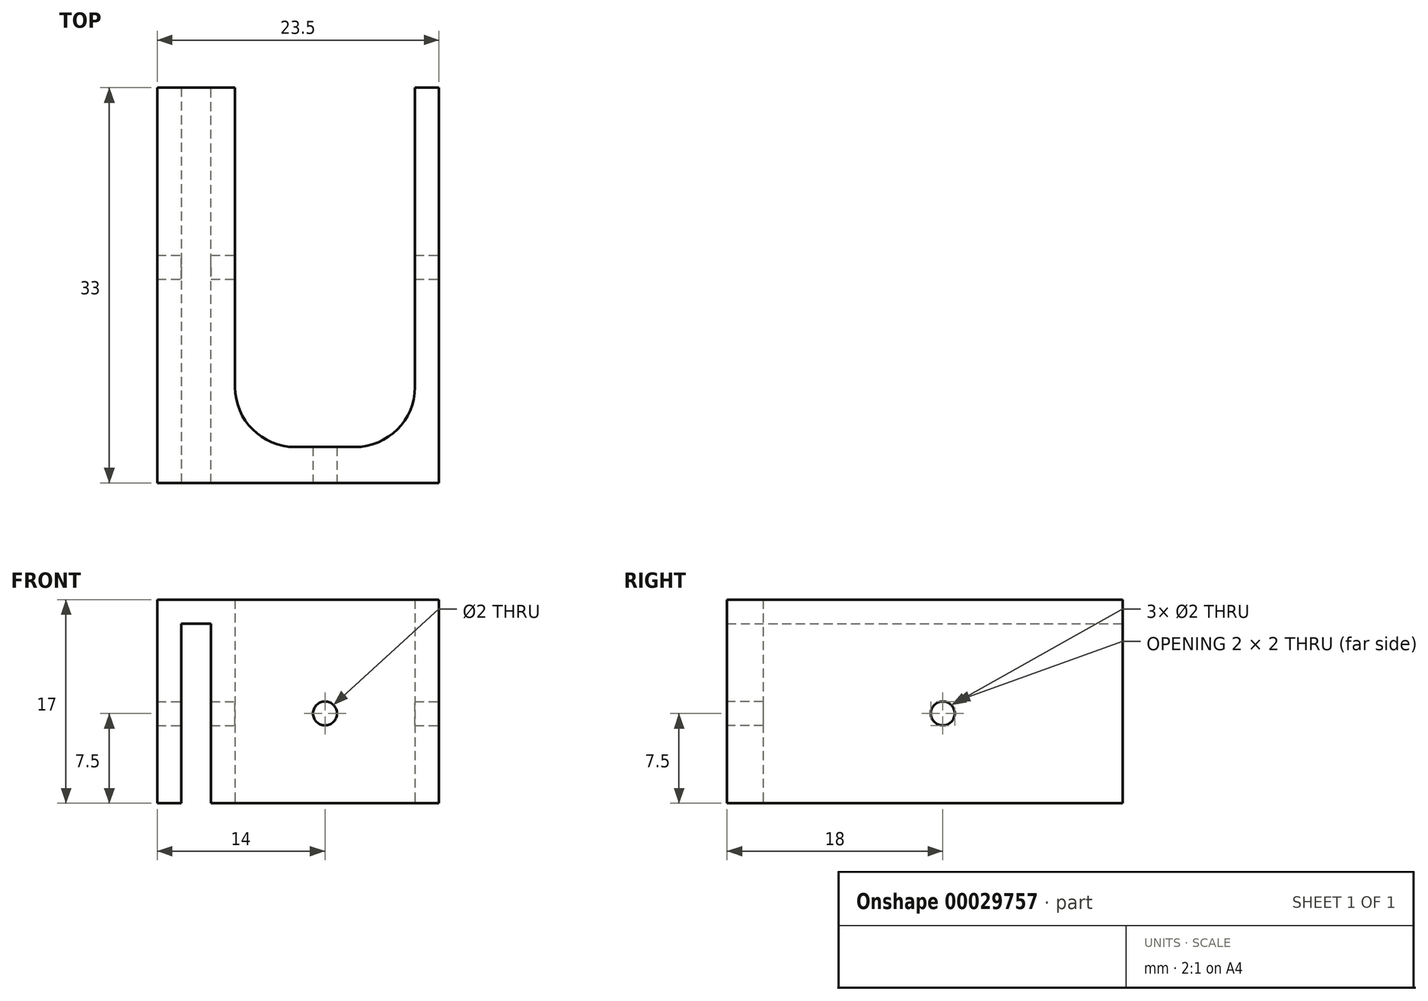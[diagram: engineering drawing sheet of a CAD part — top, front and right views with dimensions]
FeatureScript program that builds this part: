
annotation { "Feature Type Name" : "Feature", "Feature Type Description" : "" }
export const myFeature = defineFeature(function(context is Context, id is Id, definition is map)
    precondition{}
    {
        {
            var Q0;
            Q0=qCreatedBy(makeId("Top.planeOp"),FACE);
            var sketch = newSketch(context, id + "F0", { "sketchPlane" : qUnion([Q0])});
            skLineSegment(sketch, "E0.top", {"start": v(0, 33) * mm, "end": v(-2, 33) * mm});
            skLineSegment(sketch, "E0.left", {"start": v(0, 0) * mm, "end": v(0, 33) * mm});
            skLineSegment(sketch, "E0.right", {"start": v(-19, 6) * mm, "end": v(-19, 33) * mm});
            skLineSegment(sketch, "E1.top", {"start": v(-17, 3) * mm, "end": v(-2, 3) * mm});
            skLineSegment(sketch, "E1.left", {"start": v(-17, 33) * mm, "end": v(-17, 3) * mm});
            skLineSegment(sketch, "E1.right", {"start": v(-2, 33) * mm, "end": v(-2, 3) * mm});
            skLineSegment(sketch, "E2.trimOffspring", {"start": v(-17, 33) * mm, "end": v(-19, 33) * mm});
            skLineSegment(sketch, "E3", {"start": v(-19, 0) * mm, "end": v(0, 0) * mm});
            skPoint(sketch, "E4.end.orphan", {"position": v(12, 0) * mm});
            skPoint(sketch, "E5.end.orphan", {"position": v(-31, 0) * mm});
            skLineSegment(sketch, "E6", {"start": v(-19, 0) * mm, "end": v(-23.5, 0) * mm});
            skLineSegment(sketch, "E7", {"start": v(-23.5, 0) * mm, "end": v(-23.5, 33) * mm});
            skLineSegment(sketch, "E8", {"start": v(-23.5, 33) * mm, "end": v(-21.5, 33) * mm});
            skLineSegment(sketch, "E9", {"start": v(-21.5, 33) * mm, "end": v(-21.5, 6) * mm});
            skLineSegment(sketch, "E10", {"start": v(-19, 6) * mm, "end": v(-21.5, 6) * mm});
            skPoint(sketch, "E11.orphan", {"position": v(-21.5, 3) * mm});
            skSolve(sketch);
        }
        {
            var Q0;
            Q0=makeQuery(id+"F0.imprint","IMPRINT",FACE,{"disambiguationData":[TD([[makeQuery(id+"F0.imprint","IMPRINT",EDGE,{"derivedFrom":sQuery(id+"F0.wireOp",EDGE,"E0.top")}),1.0]])]});
            extrude(context, id + "F1", {"entities" : qUnion([Q0]), "depth" : 15 * mm});
        }
        {
            var Q0;
            Q0=makeQuery(id+"F1.opExtrude","SWEPT_FACE",FACE,{"disambiguationData":[OSD([sQuery(id+"F0.wireOp",EDGE,"E0.left")])]});
            var sketch = newSketch(context, id + "F2", { "sketchPlane" : qUnion([Q0])});
            skCircle(sketch, "E12", {"center": v(18, 7.5) * mm, "radius": 1 * mm});
            skSolve(sketch);
        }
        {
            var Q0;
            Q0=qSketchRegion(id+"F2",true);
            extrude(context, id + "F3", {"entities" : qUnion([Q0]), "operationType" : NewBodyOperationType.REMOVE, "oppositeDirection" : true, "depth" : 25 * mm});
        }
        {
            var Q0;
            Q0=makeQuery(id+"F1.opExtrude","SWEPT_FACE",FACE,{"disambiguationData":[OSD([sQuery(id+"F0.wireOp",EDGE,"E3"),sQuery(id+"F0.wireOp",EDGE,"E5"),sQuery(id+"F0.wireOp",EDGE,"KW2I9wrd-rldA-EDLi-8j01-u2Y36levhrCV")])]});
            var sketch = newSketch(context, id + "F4", { "sketchPlane" : qUnion([Q0])});
            skCircle(sketch, "E13", {"center": v(-9.5, 7.5) * mm, "radius": 1 * mm});
            skCircle(sketch, "E14", {"center": v(-25, 7.5) * mm, "radius": 1 * mm});
            skCircle(sketch, "E15", {"center": v(6, 7.5) * mm, "radius": 1 * mm});
            skLineSegment(sketch, "E16.0", {"start": v(12, 15) * mm, "end": v(12, 0) * mm});
            skCircle(sketch, "E17", {"center": v(-31, 7.5) * mm, "radius": 0.5 * mm});
            skCircle(sketch, "E18", {"center": v(12, 7.5) * mm, "radius": 0.5 * mm});
            skLineSegment(sketch, "E19.0", {"start": v(12, 15) * mm, "end": v(-31, 15) * mm});
            skSolve(sketch);
        }
        {
            var Q0;
            Q0=qSketchRegion(id+"F4",true);
            extrude(context, id + "F5", {"entities" : qUnion([Q0]), "operationType" : NewBodyOperationType.REMOVE, "oppositeDirection" : true, "depth" : 25 * mm});
        }
        {
            var Q0;
            Q0=makeQuery(id+"F1.opExtrude","SWEPT_EDGE",EDGE,{"disambiguationData":[OSD([sQuery(id+"F0.wireOp",EDGE,"E1.top"),sQuery(id+"F0.wireOp",EDGE,"E1.right")])]});
            var Q1;
            Q1=makeQuery(id+"F1.opExtrude","SWEPT_EDGE",EDGE,{"disambiguationData":[OSD([sQuery(id+"F0.wireOp",EDGE,"E1.top"),sQuery(id+"F0.wireOp",EDGE,"E1.left")])]});
            fillet(context, id + "F6", {"entities" : qUnion([Q0, Q1]), "radius" : 5 * mm, "tangentPropagation" : true, "allowEdgeOverflow" : false});
        }
        {
            var Q0;
            Q0=makeQuery(id+"F1.opExtrude","CAP_FACE",FACE,{"disambiguationData":[OSD([sQuery(id+"F0.wireOp",EDGE,"E0.top"),sQuery(id+"F0.wireOp",EDGE,"E0.left"),sQuery(id+"F0.wireOp",EDGE,"E0.right"),sQuery(id+"F0.wireOp",EDGE,"E1.top"),sQuery(id+"F0.wireOp",EDGE,"E1.left"),sQuery(id+"F0.wireOp",EDGE,"E1.right"),sQuery(id+"F0.wireOp",EDGE,"E2.trimOffspring"),sQuery(id+"F0.wireOp",EDGE,"E3"),sQuery(id+"F0.wireOp",EDGE,"E6"),sQuery(id+"F0.wireOp",EDGE,"E7"),sQuery(id+"F0.wireOp",EDGE,"E8"),sQuery(id+"F0.wireOp",EDGE,"E9"),sQuery(id+"F0.wireOp",EDGE,"E10")])],"isStart":false});
            var sketch = newSketch(context, id + "F7", { "sketchPlane" : qUnion([Q0])});
            skLineSegment(sketch, "E20", {"start": v(-19, 33) * mm, "end": v(-21.5, 33) * mm});
            skLineSegment(sketch, "E21.0", {"start": v(-19, 6) * mm, "end": v(-19, 33) * mm});
            skLineSegment(sketch, "E22.0", {"start": v(-21.5, 33) * mm, "end": v(-21.5, 6) * mm});
            skLineSegment(sketch, "E23.0", {"start": v(-19, 6) * mm, "end": v(-21.5, 6) * mm});
            skSolve(sketch);
        }
        {
            var Q0;
            {var subQ12=sQuery(id+"F0.wireOp",EDGE,"E0.top");Q0=makeQuery(id+"F7.imprint","IMPRINT",FACE,{"disambiguationData":[TD([[makeQuery(id+"F7.imprint","IMPRINT",EDGE,{"derivedFrom":makeQuery(id+"F1.opExtrude","CAP_EDGE",EDGE,{"disambiguationData":[OSD([subQ12])],"isStart":false})}),1.0]])]});}
            extrude(context, id + "F8", {"entities" : qUnion([Q0]), "operationType" : NewBodyOperationType.ADD, "depth" : 2 * mm});
        }
        {
            var Q0;
            Q0=qSketchRegion(id+"F7",true);
            extrude(context, id + "F9", {"entities" : qUnion([Q0]), "operationType" : NewBodyOperationType.ADD, "depth" : 2 * mm});
        }
        {
            var Q0;
            Q0=makeQuery(id+"F8.boolean.opBoolean","MERGE",FACE,{"derivedFrom":[makeQuery(id+"F1.opExtrude","SWEPT_FACE",FACE,{"disambiguationData":[OSD([sQuery(id+"F0.wireOp",EDGE,"E10")])]}),makeQuery(id+"F8.opExtrude","SWEPT_FACE",FACE,{"disambiguationData":[OSD([sQuery(id+"F7.wireOp",EDGE,"E23.0")])]})]});
            extrude(context, id + "F10", {"entities" : qUnion([Q0]), "operationType" : NewBodyOperationType.REMOVE, "oppositeDirection" : true, "depth" : 25 * mm});
        }
    });
